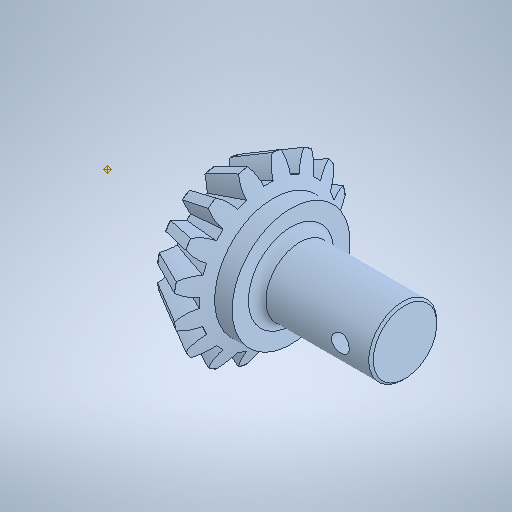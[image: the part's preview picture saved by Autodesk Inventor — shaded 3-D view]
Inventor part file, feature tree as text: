
AUTODESK INVENTOR PART (.ipt)
format: ipt  version: 2025.1 (Build 291241000, 241)  size: 7,874,560 bytes
history: native  units: in
note: dims shown in document units (in); Inventor stores cm internally (conversion verified against a paired STEP export)
features: plane x6, sketch x6, extrude x3, revolve x2, fillet x2, pattern_circular x1, chamfer x1
ambient origin geometry x8: Origin, YZ Plane, XZ Plane, XY Plane, X Axis, Y Axis, Z Axis, Center Point
bodies: Solid1 (feature_tree)
feature tree (21):
  revolve  "Revolution1"  [1 undecoded]
  plane  "Work Plane2"
  plane  "Work Plane5"
  extrude  "Extrusion6"  Depth=0.0945in
  pattern_circular  "Circular Pattern2"  Count=4  [1 undecoded]
  plane  "Work Plane7"
  plane  "Work Plane6"
  sketch  "Sketch11"  dims[d5=0.3937in d9=1.5748in]
  revolve  "Revolution3"  [1 undecoded]
  chamfer  "Chamfer3"  Distance=0.7043in
  fillet  "Congé5"  Radius=1.4085in
  extrude  "Extrusion15"  Depth=0.1969in
  extrude  "Extrusion17"  Depth=0.1969in
  fillet  "Congé7"  Radius=1.5748in
  sketch  "Sketch1"  dims[d0=3.1496in d1=0.1825in]
  plane  "Work Plane1"
  plane  "Work Plane4"
  sketch  "Sketch8"  dims[d2=0.0787in d3=0.0945in]
  sketch  "Sketch12"  dims[d10=90.0deg d11=0.162in d12=1.5748in d43=0.7043in d47=1.4085in d48=1.4961in d49=0.3543in d50=-0.4359in d51=1.5748in d53=0.0787in d54=0.0691in d56=0.4724in d57=-0.0197in d58=6.2992in d59=360.0deg d63=0.1297in d82=0.0875in d83=-0.0875in d84=1.4086in d89=1.0236in d90=0.4331in d91=0.1181in d92=90.0deg d96=0.3051in d105=0.0197in d106=0.0787in d107=45.0deg d130=0.1575in d131=0.5292in d146=0.0787in d147=0.2756in d148=0.1575in d149=0.0in d150=0.0in d154=0.3228in d155=0.3937in d156=0.0in d158=0.1969in]
  sketch  "Esquisse23"
  sketch  "Esquisse25"
note: 3 required parameter values undecoded (feature->parameter linkage not recoverable at this tier; creation-order binding heuristic only, values carry confidence <= 0.55)